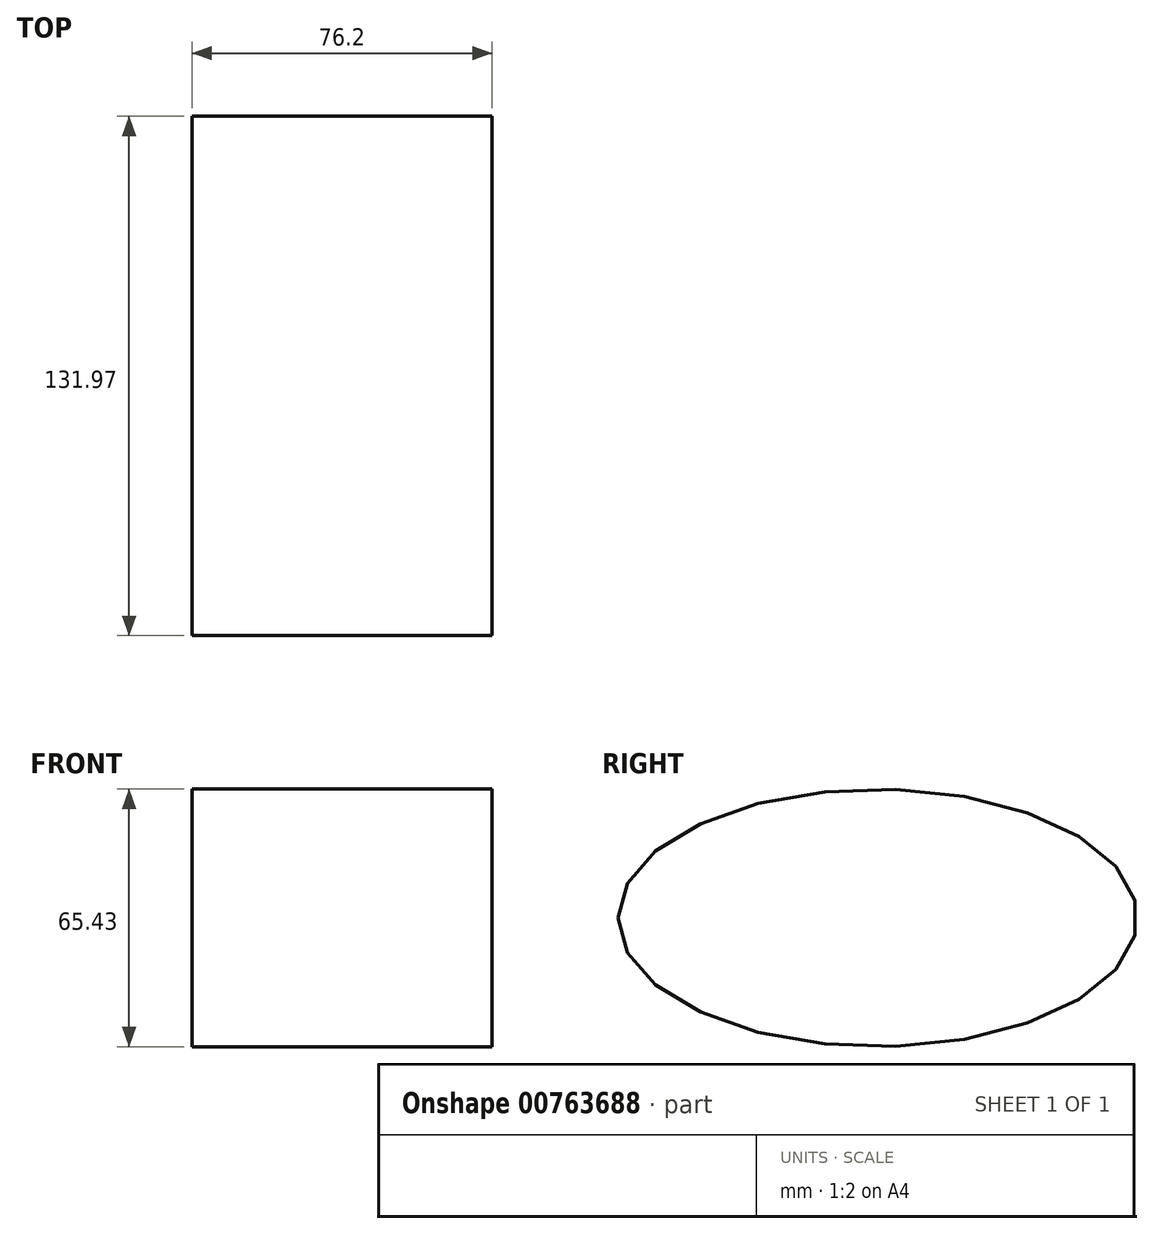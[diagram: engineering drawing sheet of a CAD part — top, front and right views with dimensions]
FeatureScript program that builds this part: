
annotation { "Feature Type Name" : "Feature", "Feature Type Description" : "" }
export const myFeature = defineFeature(function(context is Context, id is Id, definition is map)
    precondition{}
    {
        {
            var Q0;
            Q0=qCreatedBy(makeId("Right.planeOp"),FACE);
            var sketch = newSketch(context, id + "F0", { "sketchPlane" : qUnion([Q0])});
            skEllipse(sketch, "E0", {"center": v(17.71, 10.1) * mm, "majorRadius": 65.99 * mm, "minorRadius": 32.72 * mm, "majorAxis": v(-1, 0)});
            skSolve(sketch);
        }
        {
            var Q0;
            Q0=sQuery(id+"F0.wireOp",EDGE,"E0");
            extrude(context, id + "F1", {"bodyType" : ToolBodyType.SURFACE, "surfaceEntities" : qUnion([Q0]), "depth" : 76.2 * mm, "offsetDistance" : 25.4 * mm});
        }
    });
